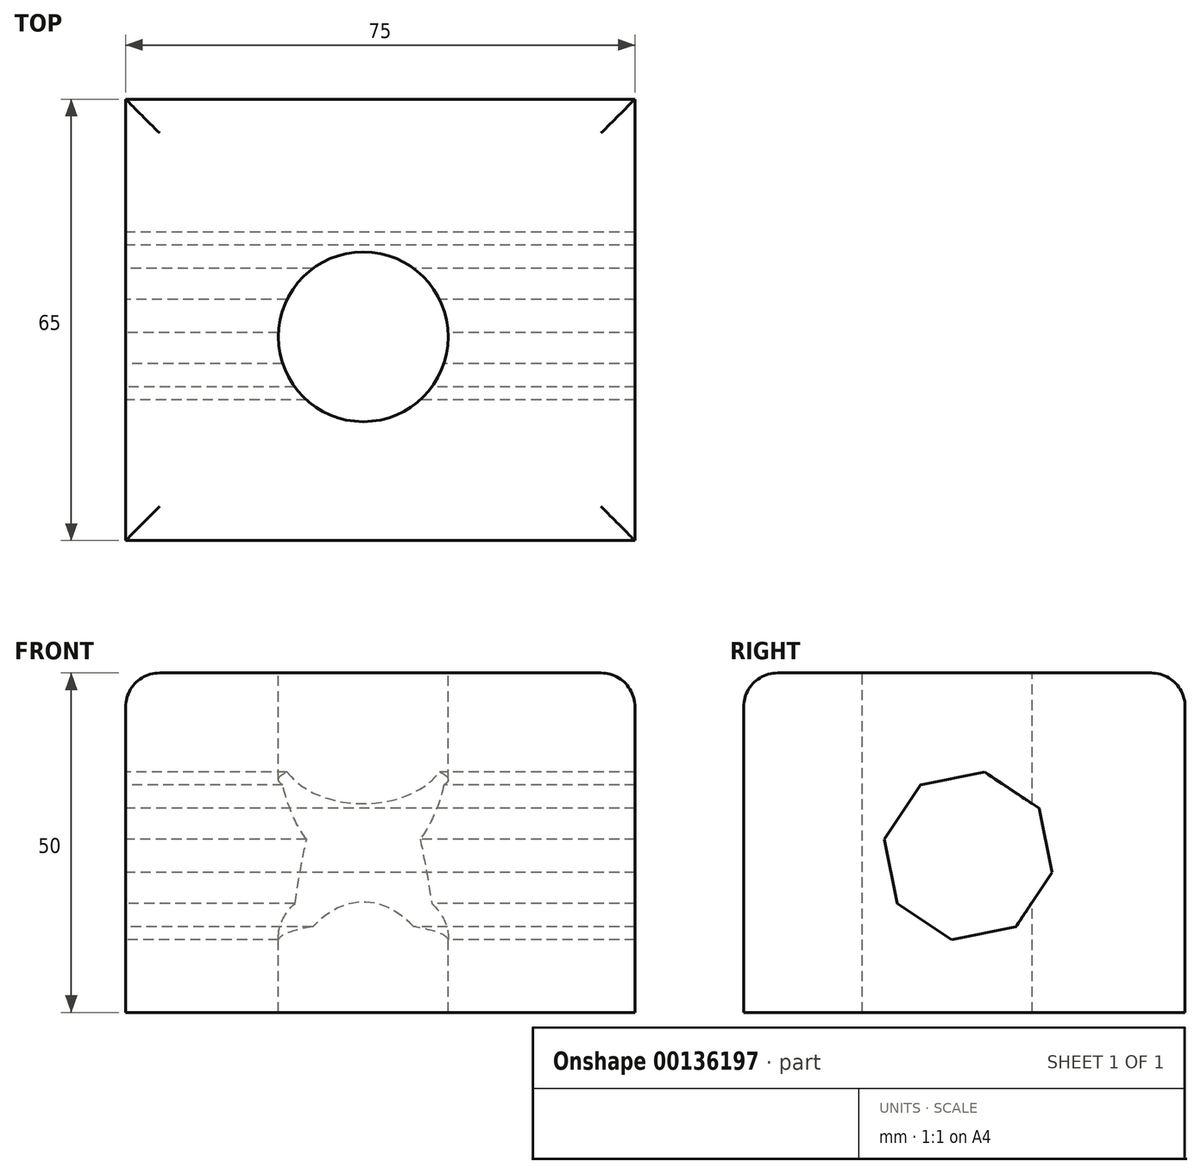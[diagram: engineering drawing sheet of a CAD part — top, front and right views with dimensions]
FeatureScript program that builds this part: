
annotation { "Feature Type Name" : "Feature", "Feature Type Description" : "" }
export const myFeature = defineFeature(function(context is Context, id is Id, definition is map)
    precondition{}
    {
        {
            var Q0;
            Q0=qCreatedBy(makeId("Front.planeOp"),FACE);
            var sketch = newSketch(context, id + "F0", { "sketchPlane" : qUnion([Q0])});
            skLineSegment(sketch, "E0.bottom", {"start": v(-37.6, 0) * mm, "end": v(37.4, 0) * mm});
            skLineSegment(sketch, "E0.top", {"start": v(-37.6, -50) * mm, "end": v(37.4, -50) * mm});
            skLineSegment(sketch, "E0.left", {"start": v(-37.6, 0) * mm, "end": v(-37.6, -50) * mm});
            skLineSegment(sketch, "E0.right", {"start": v(37.4, 0) * mm, "end": v(37.4, -50) * mm});
            skSolve(sketch);
        }
        {
            var Q0;
            Q0 = qSketchRegion(id + "F0", true);
            extrude(context, id + "F1", {"entities" : qUnion([Q0]), "depth" : 65 * mm});
        }
        {
            var Q0;
            Q0=makeQuery(id+"F1.opExtrude","CAP_EDGE",EDGE,{"disambiguationData":[OSD([sQuery(id+"F0.wireOp",EDGE,"E0.bottom")])],"isStart":false});
            var Q1;
            Q1=makeQuery(id+"F1.opExtrude","SWEPT_EDGE",EDGE,{"disambiguationData":[OSD([sQuery(id+"F0.wireOp",EDGE,"E0.bottom"),sQuery(id+"F0.wireOp",EDGE,"E0.left")])]});
            var Q2;
            Q2=makeQuery(id+"F1.opExtrude","CAP_EDGE",EDGE,{"disambiguationData":[OSD([sQuery(id+"F0.wireOp",EDGE,"E0.bottom")])],"isStart":true});
            var Q3;
            Q3=makeQuery(id+"F1.opExtrude","SWEPT_FACE",FACE,{"disambiguationData":[OSD([sQuery(id+"F0.wireOp",EDGE,"E0.bottom")])]});
            fillet(context, id + "F2", {"entities" : qUnion([Q0, Q1, Q2, Q3]), "radius" : 5 * mm, "tangentPropagation" : true, "allowEdgeOverflow" : false});
        }
        {
            var Q0;
            Q0=makeQuery(id+"F1.opExtrude","SWEPT_FACE",FACE,{"disambiguationData":[OSD([sQuery(id+"F0.wireOp",EDGE,"E0.bottom")])]});
            var sketch = newSketch(context, id + "F3", { "sketchPlane" : qUnion([Q0])});
            skCircle(sketch, "E1", {"center": v(-2.6, -35) * mm, "radius": 12.5 * mm});
            skSolve(sketch);
        }
        {
            var Q0;
            Q0=makeQuery(id+"F3.imprint","IMPRINT",FACE,{"disambiguationData":[TD([[makeQuery(id+"F3.imprint","IMPRINT",EDGE,{"derivedFrom":sQuery(id+"F3.wireOp",EDGE,"E1")}),1.0]])]});
            extrude(context, id + "F4", {"entities" : qUnion([Q0]), "operationType" : NewBodyOperationType.REMOVE, "endBound" : BoundingType.THROUGH_ALL, "oppositeDirection" : true, "depth" : 25 * mm});
        }
        {
            var Q0;
            Q0=makeQuery(id+"F1.opExtrude","SWEPT_FACE",FACE,{"disambiguationData":[OSD([sQuery(id+"F0.wireOp",EDGE,"E0.left")])]});
            var sketch = newSketch(context, id + "F5", { "sketchPlane" : qUnion([Q0])});
            skCircle(sketch, "E2.cCircle", {"center": v(31.95, -26.96) * mm, "radius": 11.63 * mm, "construction": true});
            skLineSegment(sketch, "E2.0", {"start": v(42.4, -33.96) * mm, "end": v(34.4, -39.3) * mm});
            skLineSegment(sketch, "E2.1", {"start": v(34.4, -39.3) * mm, "end": v(24.95, -37.41) * mm});
            skLineSegment(sketch, "E2.2", {"start": v(24.95, -37.41) * mm, "end": v(19.6, -29.4) * mm});
            skLineSegment(sketch, "E2.3", {"start": v(19.6, -29.4) * mm, "end": v(21.5, -19.96) * mm});
            skLineSegment(sketch, "E2.4", {"start": v(21.5, -19.96) * mm, "end": v(29.51, -14.61) * mm});
            skLineSegment(sketch, "E2.5", {"start": v(29.51, -14.61) * mm, "end": v(38.96, -16.5) * mm});
            skLineSegment(sketch, "E2.6", {"start": v(38.96, -16.5) * mm, "end": v(44.3, -24.52) * mm});
            skLineSegment(sketch, "E2.7", {"start": v(44.3, -24.52) * mm, "end": v(42.4, -33.96) * mm});
            skPoint(sketch, "E2.0.midPoint", {"position": v(38.4, -36.63) * mm});
            skSolve(sketch);
        }
        {
            var Q0;
            Q0 = qSketchRegion(id + "F5", true);
            extrude(context, id + "F6", {"entities" : qUnion([Q0]), "operationType" : NewBodyOperationType.REMOVE, "endBound" : BoundingType.THROUGH_ALL, "oppositeDirection" : true, "depth" : 25 * mm});
        }
    });
